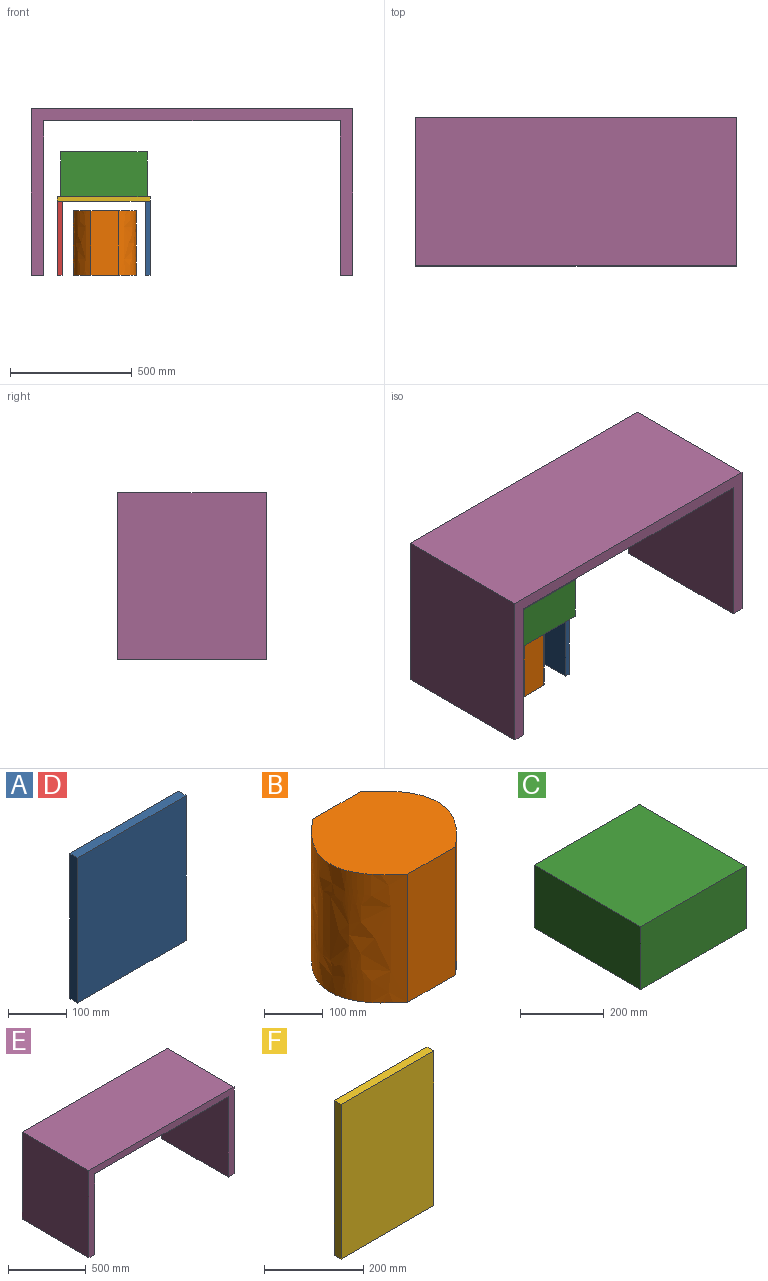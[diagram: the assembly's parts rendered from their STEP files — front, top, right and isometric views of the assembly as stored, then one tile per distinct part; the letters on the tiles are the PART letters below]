
ASSEMBLY  parts=6 mates=5
PART A: 6 faces, bbox 263.5x19.1x304.8 mm
  f0: plane 304.8x19.05mm, normal (1,0,0), area 5806.4mm2, adj f1,f3,f4,f5
  f1: plane 304.8x263.53mm, normal (0,1,0), area 80322.4mm2, adj f0,f2,f4,f5
  f2: plane 304.8x19.05mm, normal (-1,0,0), area 5806.4mm2, adj f1,f3,f4,f5
  f3: plane 304.8x263.53mm, normal (0,-1,0), area 80322.4mm2, adj f0,f2,f4,f5
  f4: plane 263.53x19.05mm, normal (0,0,-1), area 5020.2mm2, adj f0,f1,f2,f3
  f5: plane 263.53x19.05mm, normal (0,0,1), area 5020.2mm2, adj f0,f1,f2,f3
PART B: 6 faces, bbox 312.8x228.6x266.7 mm
  f0: extruded ~266.7x228.6mm, area 74584.9mm2, adj f1,f3,f4,f5
  f1: plane 266.7x114.3mm, normal (0,1,0), area 30483.8mm2, adj f0,f2,f4,f5
  f2: extruded ~266.7x228.6mm, area 74584.9mm2, adj f1,f3,f4,f5
  f3: plane 266.7x114.3mm, normal (0,-1,0), area 30483.8mm2, adj f0,f2,f4,f5
  f4: plane 312.77x228.6mm, normal (0,0,-1), area 48126.6mm2, adj f0,f1,f2,f3
  f5: plane 312.77x228.6mm, normal (0,0,1), area 48126.6mm2, adj f0,f1,f2,f3
PART C: 6 faces, bbox 355.6x362x184.2 mm
  f0: plane 361.95x184.15mm, normal (-1,0,0), area 66653.1mm2, adj f1,f3,f4,f5
  f1: plane 361.95x355.6mm, normal (0,0,-1), area 128709.4mm2, adj f0,f2,f4,f5
  f2: plane 361.95x184.15mm, normal (1,0,0), area 66653.1mm2, adj f1,f3,f4,f5
  f3: plane 361.95x355.6mm, normal (0,0,1), area 128709.4mm2, adj f0,f2,f4,f5
  f4: plane 355.6x184.15mm, normal (0,1,0), area 65483.7mm2, adj f0,f1,f2,f3
  f5: plane 355.6x184.15mm, normal (0,-1,0), area 65483.7mm2, adj f0,f1,f2,f3
PART D: same geometry as A
PART E: 10 faces, bbox 1320.8x609.6x685.8 mm
  f0: plane 685.8x609.6mm, normal (-1,0,0), area 418063.7mm2, adj f1,f7,f8,f9
  f1: plane 609.6x50.8mm, normal (0,0,-1), area 30967.7mm2, adj f0,f2,f8,f9
  f2: plane 635x609.6mm, normal (1,0,0), area 387096mm2, adj f1,f3,f8,f9
  f3: plane 1219.2x609.6mm, normal (0,0,-1), area 743224.3mm2, adj f2,f4,f8,f9
  f4: plane 635x609.6mm, normal (-1,0,0), area 387096mm2, adj f3,f5,f8,f9
  f5: plane 609.6x50.8mm, normal (0,0,-1), area 30967.7mm2, adj f4,f6,f8,f9
  f6: plane 685.8x609.6mm, normal (1,0,0), area 418063.7mm2, adj f5,f7,f8,f9
  f7: plane 1320.8x609.6mm, normal (0,0,1), area 805159.7mm2, adj f0,f6,f8,f9
  f8: plane 1320.8x685.8mm, normal (0,-1,0), area 131612.6mm2, adj f0,f1,f2,f3,f4,f5,f6,f7
  f9: plane 1320.8x685.8mm, normal (0,1,0), area 131612.6mm2, adj f0,f1,f2,f3,f4,f5,f6,f7
PART F: 6 faces, bbox 263.5x19.1x381 mm
  f0: plane 381x19.05mm, normal (1,0,0), area 7258mm2, adj f1,f3,f4,f5
  f1: plane 381x263.53mm, normal (0,1,0), area 100403mm2, adj f0,f2,f4,f5
  f2: plane 381x19.05mm, normal (-1,0,0), area 7258mm2, adj f1,f3,f4,f5
  f3: plane 381x263.53mm, normal (0,-1,0), area 100403mm2, adj f0,f2,f4,f5
  f4: plane 263.53x19.05mm, normal (0,0,-1), area 5020.2mm2, adj f0,f1,f2,f3
  f5: plane 263.53x19.05mm, normal (0,0,1), area 5020.2mm2, adj f0,f1,f2,f3
PLACE A rot(axis=(0,0,1),90deg) t=(118.06,124.11,304.8)mm
PLACE B t=(348.92,-118.6,266.7)mm
PLACE C t=(-182.24,-180.98,323.85)mm
PLACE D rot(axis=(0,0,1),90deg) t=(-243.89,124.11,304.8)mm
PLACE E t=(-405.3,304.8,766.88)mm
PLACE F rot(axis=(0.58,0.58,0.58),120deg) t=(186.06,131.76,427.15)mm
MATE fastened D.f5 <-> F.f3  axis (0,0,1) through (-194.94,0,304.8)mm
MATE planar B.f4 <-> E.f1  axis (0,0,-1) through (0,0,0)mm
MATE fastened A.f5 <-> F.f3  axis (0,0,1) through (186.06,0,304.8)mm
MATE planar B.f4 <-> D.f4  axis (0,0,-1) through (0,0,0)mm
MATE fastened C.f1 <-> F.f1  axis (0,0,-1) through (-4.45,0,323.85)mm
